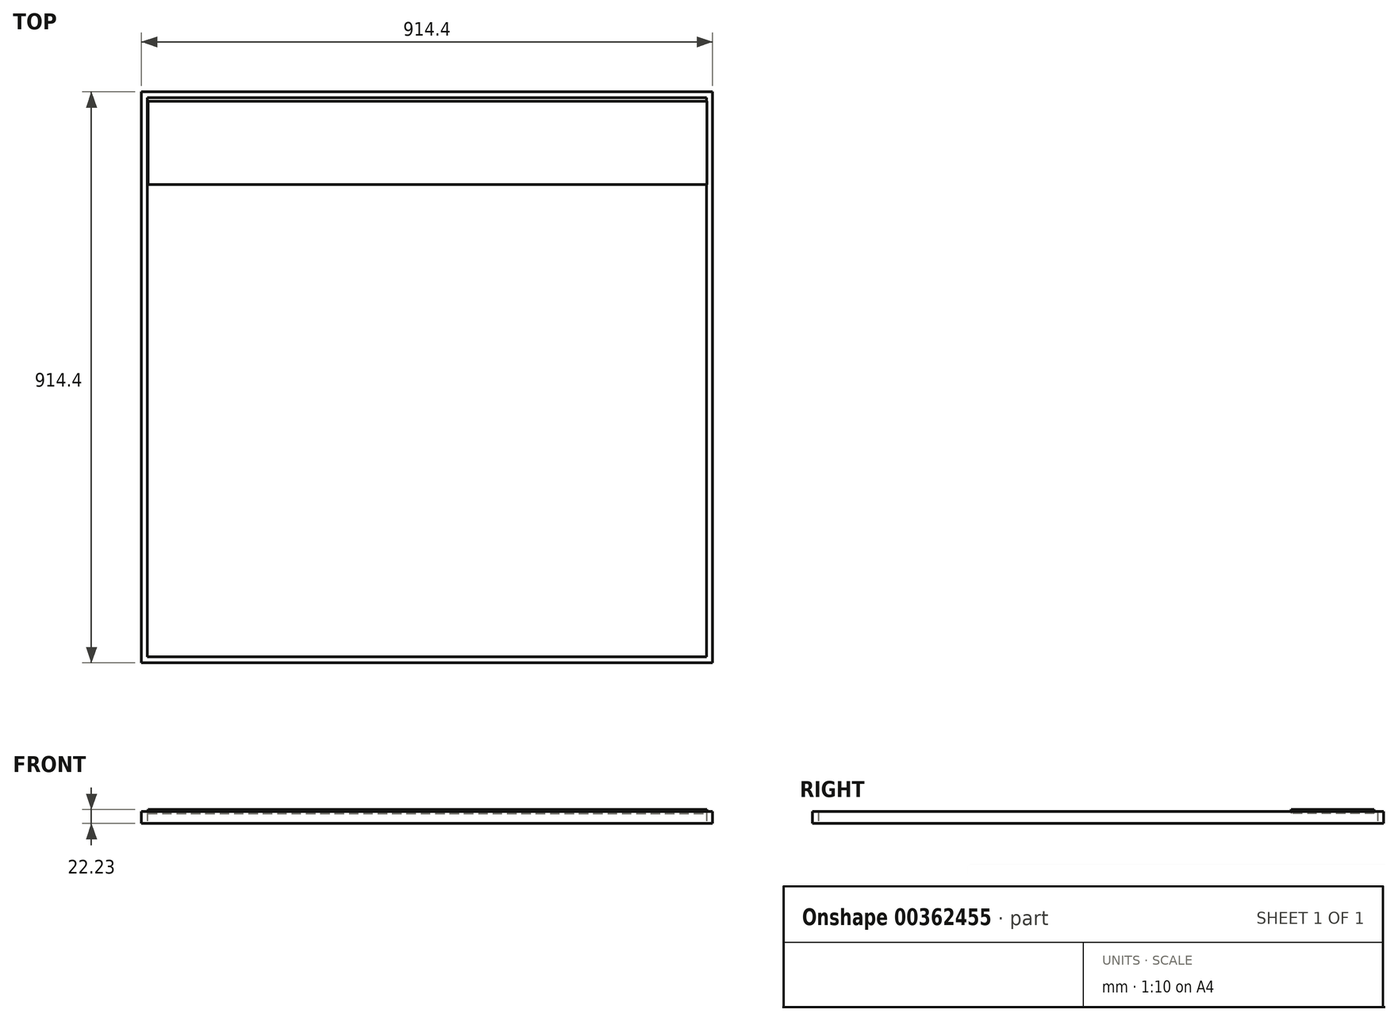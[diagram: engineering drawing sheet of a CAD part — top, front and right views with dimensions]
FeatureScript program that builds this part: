
annotation { "Feature Type Name" : "Feature", "Feature Type Description" : "" }
export const myFeature = defineFeature(function(context is Context, id is Id, definition is map)
    precondition{}
    {
        {
            var Q0;
            Q0=qCreatedBy(makeId("Top.planeOp"),FACE);
            var sketch = newSketch(context, id + "F0", { "sketchPlane" : qUnion([Q0])});
            skLineSegment(sketch, "E0.bottom", {"start": v(457.2, 457.2) * mm, "end": v(-457.2, 457.2) * mm});
            skLineSegment(sketch, "E0.top", {"start": v(457.2, -457.2) * mm, "end": v(-457.2, -457.2) * mm});
            skLineSegment(sketch, "E0.left", {"start": v(457.2, 457.2) * mm, "end": v(457.2, -457.2) * mm});
            skLineSegment(sketch, "E0.right", {"start": v(-457.2, 457.2) * mm, "end": v(-457.2, -457.2) * mm});
            skPoint(sketch, "E0.middle", {"position": v(0, 0) * mm});
            skLineSegment(sketch, "E1", {"start": v(186.25, 457.2) * mm, "end": v(186.25, 438.15) * mm});
            skLineSegment(sketch, "E2.bottom", {"start": v(447.68, 447.68) * mm, "end": v(-447.68, 447.68) * mm});
            skLineSegment(sketch, "E2.top", {"start": v(447.68, -447.67) * mm, "end": v(-447.68, -447.68) * mm});
            skLineSegment(sketch, "E2.left", {"start": v(447.68, 447.68) * mm, "end": v(447.68, -447.67) * mm});
            skLineSegment(sketch, "E2.right", {"start": v(-447.68, 447.67) * mm, "end": v(-447.68, -447.68) * mm});
            skSolve(sketch);
        }
        {
            var Q0;
            Q0 = qSketchRegion(id + "F0", true);
            extrude(context, id + "F1", {"entities" : qUnion([Q0]), "depth" : 19.05 * mm});
        }
        {
            var Q0;
            Q0=makeQuery(id+"F1.opExtrude","CAP_FACE",FACE,{"disambiguationData":[OSD([sQuery(id+"F0.wireOp",EDGE,"E0.bottom"),sQuery(id+"F0.wireOp",EDGE,"E0.top"),sQuery(id+"F0.wireOp",EDGE,"E0.left"),sQuery(id+"F0.wireOp",EDGE,"E0.right"),sQuery(id+"F0.wireOp",EDGE,"E2.bottom"),sQuery(id+"F0.wireOp",EDGE,"E2.top"),sQuery(id+"F0.wireOp",EDGE,"E2.left"),sQuery(id+"F0.wireOp",EDGE,"E2.right")])],"isStart":false});
            var sketch = newSketch(context, id + "F2", { "sketchPlane" : qUnion([Q0])});
            skLineSegment(sketch, "E3.bottom", {"start": v(447.67, 288.53) * mm, "end": v(-447.67, 288.53) * mm});
            skLineSegment(sketch, "E3.top", {"start": v(447.68, 307.58) * mm, "end": v(-447.68, 307.58) * mm});
            skLineSegment(sketch, "E3.left", {"start": v(447.68, 288.53) * mm, "end": v(447.68, 307.58) * mm});
            skLineSegment(sketch, "E3.right", {"start": v(-447.68, 288.53) * mm, "end": v(-447.68, 307.58) * mm});
            skSolve(sketch);
        }
        {
            var Q0;
            Q0 = qSketchRegion(id + "F2", true);
            var sketch = newSketch(context, id + "F3", { "sketchPlane" : qUnion([Q0])});
            skSolve(sketch);
        }
        {
            var Q0;
            {var subQ0=sQuery(id+"F2.wireOp",EDGE,"E3.right");Q0=makeQuery(id+"F3.imprint","IMPRINT",FACE,{"disambiguationData":[TD([[makeQuery(id+"F3.imprint","IMPRINT",EDGE,{"derivedFrom":makeQuery(id+"F2.imprint","IMPRINT",EDGE,{"derivedFrom":subQ0})}),1.0]])]});}
            var sketch = newSketch(context, id + "F4", { "sketchPlane" : qUnion([Q0])});
            skSolve(sketch);
        }
        {
            var Q0;
            Q0=makeQuery(id+"F2.imprint","IMPRINT",FACE,{"disambiguationData":[TD([[makeQuery(id+"F2.imprint","IMPRINT",EDGE,{"derivedFrom":sQuery(id+"F2.wireOp",EDGE,"E3.bottom")}),-1.0]])]});
            var Q1;
            Q1 = qSketchRegion(id + "F2", true);
            extrude(context, id + "F5", {"entities" : qUnion([Q0, Q1]), "depth" : 19.05 * mm});
        }
        {
            var Q0;
            Q0=makeQuery(id+"F5.opExtrude","CAP_FACE",FACE,{"disambiguationData":[OSD([sQuery(id+"F2.wireOp",EDGE,"E3.bottom"),sQuery(id+"F2.wireOp",EDGE,"E3.top"),sQuery(id+"F2.wireOp",EDGE,"E3.left"),sQuery(id+"F2.wireOp",EDGE,"E3.right")])],"isStart":false});
            extrude(context, id + "F6", {"entities" : qUnion([Q0]), "operationType" : NewBodyOperationType.REMOVE, "oppositeDirection" : true, "depth" : 38.1 * mm});
        }
        {
            var Q0;
            Q0=makeQuery(id+"F3.imprint","IMPRINT",FACE,{"disambiguationData":[TD([[makeQuery(id+"F3.imprint","IMPRINT",EDGE,{"derivedFrom":makeQuery(id+"F2.imprint","IMPRINT",EDGE,{"derivedFrom":sQuery(id+"F2.wireOp",EDGE,"E3.bottom")})}),-1.0]])]});
            extrude(context, id + "F7", {"entities" : qUnion([Q0]), "operationType" : NewBodyOperationType.REMOVE, "oppositeDirection" : true, "depth" : 19.05 * mm});
        }
        {
            var Q0;
            Q0=makeQuery(id+"F4.imprint","IMPRINT",FACE,{"disambiguationData":[TD([[makeQuery(id+"F4.imprint","IMPRINT",EDGE,{"derivedFrom":makeQuery(id+"F3.imprint","IMPRINT",EDGE,{"derivedFrom":makeQuery(id+"F2.imprint","IMPRINT",EDGE,{"derivedFrom":sQuery(id+"F2.wireOp",EDGE,"E3.bottom")})})}),-1.0]])]});
            extrude(context, id + "F8", {"entities" : qUnion([Q0]), "operationType" : NewBodyOperationType.REMOVE, "oppositeDirection" : true, "depth" : 127 * mm});
        }
        {
            var Q0;
            Q0 = qSketchRegion(id + "F2", true);
            var Q1;
            Q1=makeQuery(id+"F2.imprint","IMPRINT",FACE,{"disambiguationData":[TD([[makeQuery(id+"F2.imprint","IMPRINT",EDGE,{"derivedFrom":sQuery(id+"F2.wireOp",EDGE,"E3.bottom")}),-1.0]])]});
            var Q2;
            Q2=sQuery(id+"F2.wireOp",EDGE,"E3.bottom");
            var Q3;
            Q3=sQuery(id+"F2.wireOp",EDGE,"E3.top");
            extrude(context, id + "F9", {"entities" : qUnion([Q0, Q1]), "bodyType" : ToolBodyType.SURFACE, "surfaceEntities" : qUnion([Q2, Q3]), "oppositeDirection" : true, "depth" : 19.05 * mm});
        }
        {
            var Q0;
            Q0=makeQuery(id+"F2.imprint","IMPRINT",FACE,{"disambiguationData":[TD([[makeQuery(id+"F2.imprint","IMPRINT",EDGE,{"derivedFrom":sQuery(id+"F2.wireOp",EDGE,"E3.bottom")}),-1.0]])]});
            var sketch = newSketch(context, id + "F10", { "sketchPlane" : qUnion([Q0])});
            skLineSegment(sketch, "E4.bottom", {"start": v(-449.26, 310.08) * mm, "end": v(450.28, 310.08) * mm});
            skLineSegment(sketch, "E4.top", {"start": v(-449.26, 287.56) * mm, "end": v(450.28, 287.56) * mm});
            skLineSegment(sketch, "E4.left", {"start": v(-449.26, 310.08) * mm, "end": v(-449.26, 287.56) * mm});
            skLineSegment(sketch, "E4.right", {"start": v(450.28, 310.08) * mm, "end": v(450.28, 287.56) * mm});
            skSolve(sketch);
        }
        {
            var Q0;
            Q0=makeQuery(id+"F10.imprint","IMPRINT",FACE,{"disambiguationData":[TD([[makeQuery(id+"F10.imprint","IMPRINT",EDGE,{"derivedFrom":makeQuery(id+"F2.imprint","IMPRINT",EDGE,{"derivedFrom":sQuery(id+"F2.wireOp",EDGE,"E3.bottom")})}),-1.0]])]});
            extrude(context, id + "F11", {"entities" : qUnion([Q0]), "operationType" : NewBodyOperationType.REMOVE, "oppositeDirection" : true, "depth" : 19.05 * mm});
        }
        {
            var Q0;
            {var subQ0=sQuery(id+"F2.wireOp",EDGE,"E3.bottom");Q0=makeQuery(id+"F2.imprint","IMPRINT",FACE,{"disambiguationData":[TD([[makeQuery(id+"F2.imprint","IMPRINT",EDGE,{"derivedFrom":subQ0}),1.0]])]});}
            var sketch = newSketch(context, id + "F12", { "sketchPlane" : qUnion([Q0])});
            skLineSegment(sketch, "E5.bottom", {"start": v(-447.03, 442.1) * mm, "end": v(448.32, 442.1) * mm});
            skLineSegment(sketch, "E5.top", {"start": v(-447.03, 308.75) * mm, "end": v(448.32, 308.75) * mm});
            skLineSegment(sketch, "E5.left", {"start": v(-447.03, 442.1) * mm, "end": v(-447.03, 308.75) * mm});
            skLineSegment(sketch, "E5.right", {"start": v(448.32, 442.1) * mm, "end": v(448.32, 308.75) * mm});
            skSolve(sketch);
        }
        {
            var Q0;
            Q0=makeQuery(id+"F12.imprint","IMPRINT",FACE,{"disambiguationData":[TD([[makeQuery(id+"F12.imprint","IMPRINT",EDGE,{"derivedFrom":sQuery(id+"F12.wireOp",EDGE,"E5.bottom")}),-1.0]])]});
            extrude(context, id + "F13", {"entities" : qUnion([Q0]), "operationType" : NewBodyOperationType.ADD, "endBound" : BoundingType.SYMMETRIC, "depth" : 6.35 * mm, "hasDraft" : true, "draftAngle" : 3 * degree, "draftPullDirection" : true});
        }
    });
